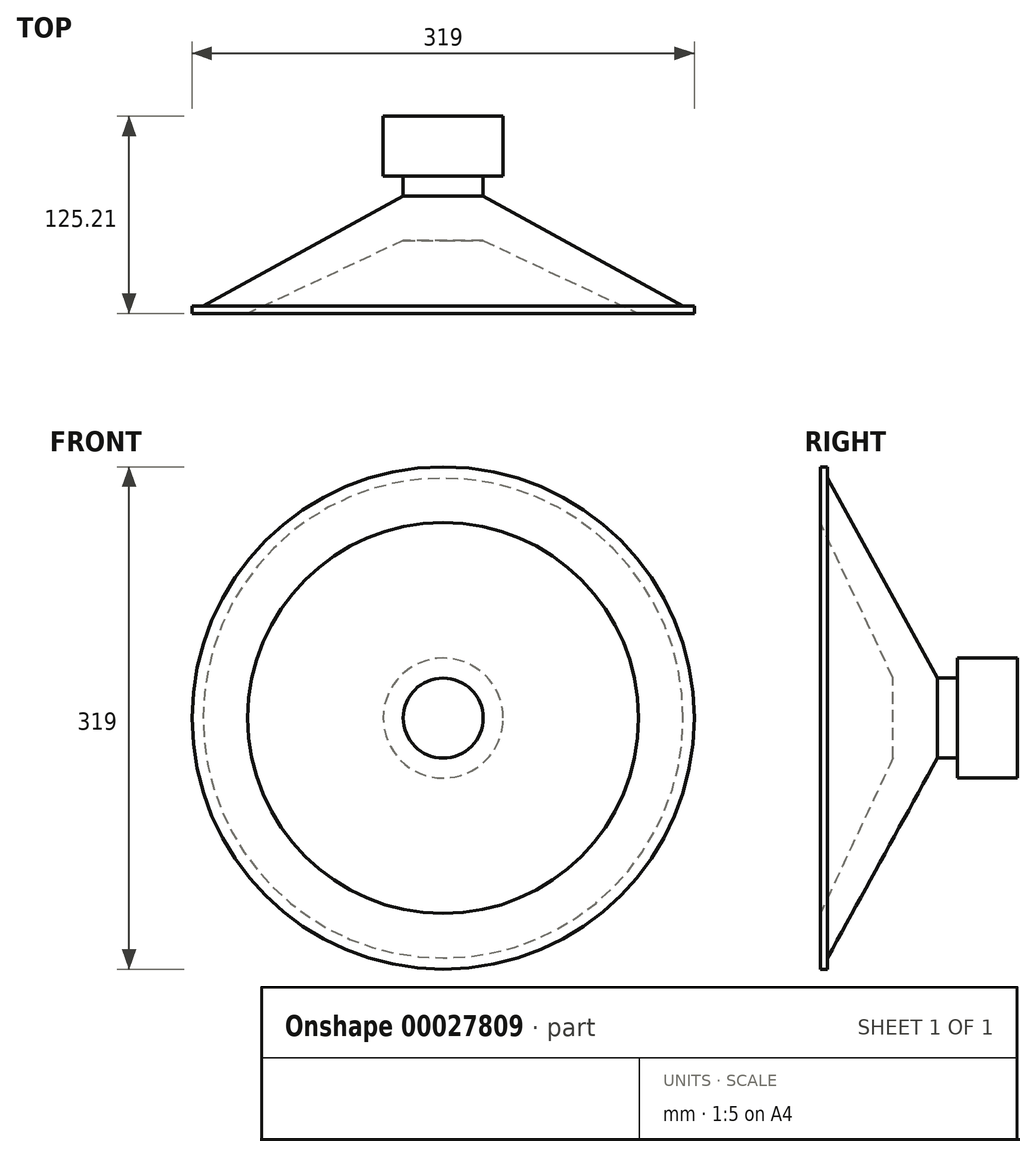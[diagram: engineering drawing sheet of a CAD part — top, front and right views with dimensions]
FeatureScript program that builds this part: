
annotation { "Feature Type Name" : "Feature", "Feature Type Description" : "" }
export const myFeature = defineFeature(function(context is Context, id is Id, definition is map)
    precondition{}
    {
        {
            var Q0;
            Q0=qCreatedBy(makeId("Top.planeOp"),FACE);
            var sketch = newSketch(context, id + "F0", { "sketchPlane" : qUnion([Q0])});
            skLineSegment(sketch, "E0", {"start": v(0, 0) * mm, "end": v(0, 38.1) * mm});
            skLineSegment(sketch, "E1", {"start": v(0, 38.1) * mm, "end": v(38.1, 38.1) * mm});
            skLineSegment(sketch, "E2", {"start": v(38.1, 38.1) * mm, "end": v(38.1, 0) * mm});
            skLineSegment(sketch, "E3", {"start": v(38.1, 0) * mm, "end": v(25.4, 0) * mm});
            skLineSegment(sketch, "E4", {"start": v(25.4, 0) * mm, "end": v(25.4, -12.7) * mm});
            skLineSegment(sketch, "E5", {"start": v(25.4, -12.7) * mm, "end": v(152.4, -82.55) * mm});
            skLineSegment(sketch, "E6", {"start": v(152.4, -82.55) * mm, "end": v(159.5, -82.55) * mm});
            skLineSegment(sketch, "E7", {"start": v(159.5, -82.55) * mm, "end": v(159.5, -87.1) * mm});
            skLineSegment(sketch, "E8", {"start": v(159.5, -87.1) * mm, "end": v(124.13, -87.1) * mm});
            skLineSegment(sketch, "E9", {"start": v(124.13, -87.1) * mm, "end": v(25.4, -40.86) * mm});
            skLineSegment(sketch, "E10", {"start": v(25.4, -40.86) * mm, "end": v(0, -40.86) * mm});
            skLineSegment(sketch, "E11", {"start": v(0, -40.86) * mm, "end": v(0, 0) * mm});
            skSolve(sketch);
        }
        {
            var Q0;
            Q0=makeQuery(id+"F0.imprint","IMPRINT",FACE,{"disambiguationData":[TD([[makeQuery(id+"F0.imprint","IMPRINT",EDGE,{"derivedFrom":sQuery(id+"F0.wireOp",EDGE,"E0")}),-1.0]])]});
            var Q1;
            Q1=sQuery(id+"F0.wireOp",EDGE,"E0");
            revolve(context, id + "F1", {"entities" : qUnion([Q0]), "axis" : qUnion([Q1]), "revolveType" : RevolveType.FULL});
        }
    });
